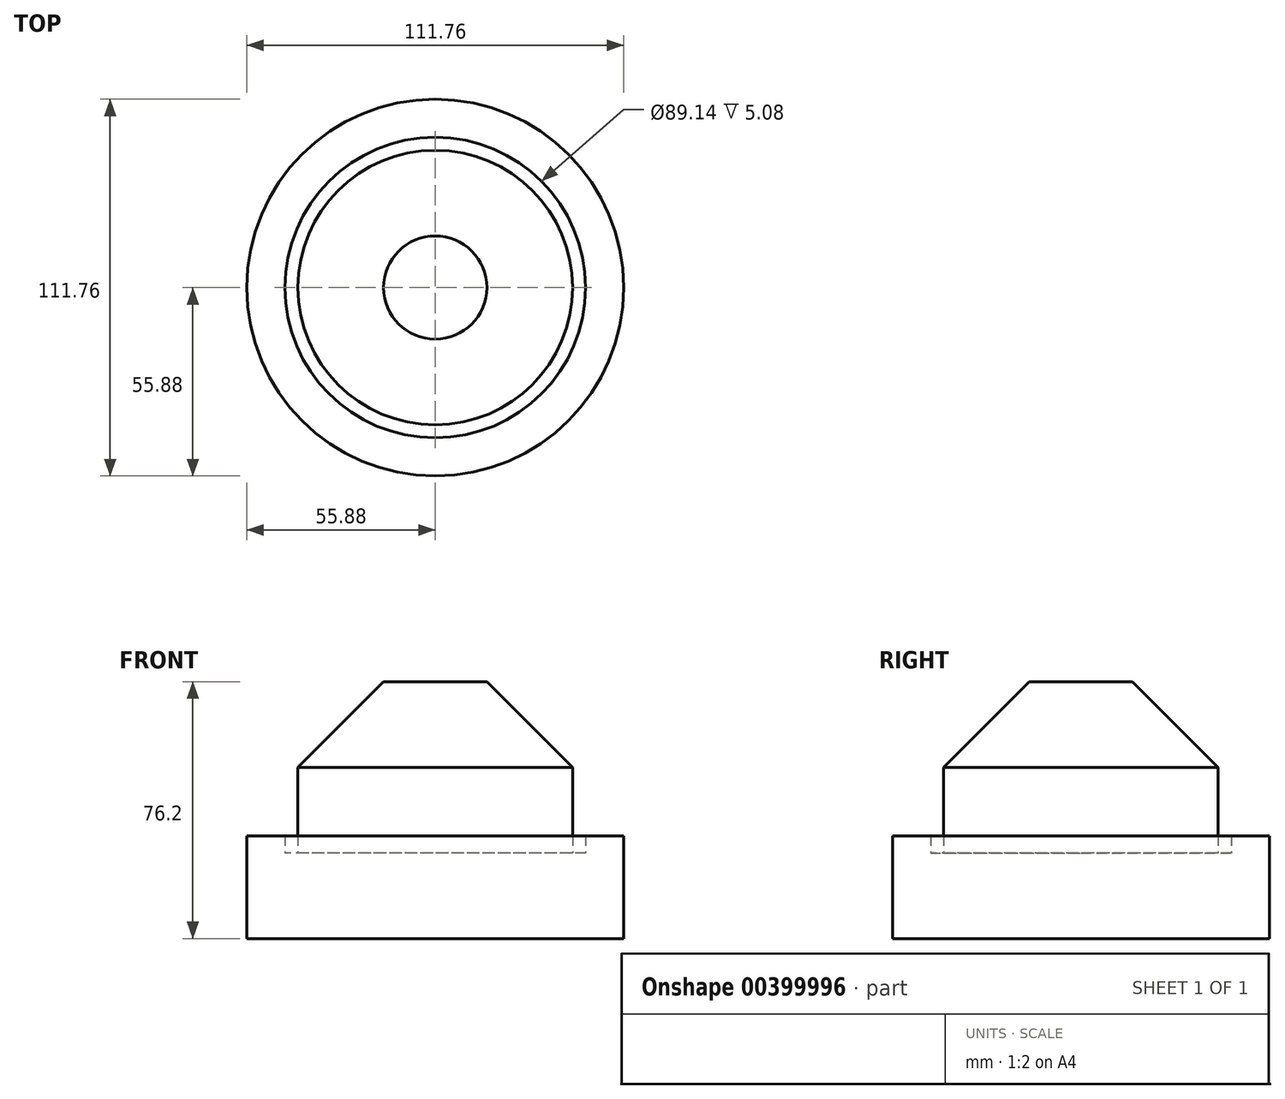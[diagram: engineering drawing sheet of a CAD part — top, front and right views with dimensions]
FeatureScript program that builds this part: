
annotation { "Feature Type Name" : "Feature", "Feature Type Description" : "" }
export const myFeature = defineFeature(function(context is Context, id is Id, definition is map)
    precondition{}
    {
        {
            var Q0;
            Q0=qCreatedBy(makeId("Top.planeOp"),FACE);
            var sketch = newSketch(context, id + "F0", { "sketchPlane" : qUnion([Q0])});
            skCircle(sketch, "E0", {"center": v(0, 0) * mm, "radius": 55.88 * mm});
            skSolve(sketch);
        }
        {
            var Q0;
            Q0 = qSketchRegion(id + "F0", true);
            extrude(context, id + "F1", {"entities" : qUnion([Q0]), "depth" : 25.4 * mm});
        }
        {
            var Q0;
            Q0=makeQuery(id+"F1.opExtrude","CAP_FACE",FACE,{"disambiguationData":[OSD([sQuery(id+"F0.wireOp",EDGE,"E0")])],"isStart":false});
            var sketch = newSketch(context, id + "F2", { "sketchPlane" : qUnion([Q0])});
            skCircle(sketch, "E1", {"center": v(0, 0) * mm, "radius": 44.57 * mm});
            skSolve(sketch);
        }
        {
            var Q0;
            Q0=makeQuery(id+"F2.imprint","IMPRINT",FACE,{"disambiguationData":[TD([[makeQuery(id+"F2.imprint","IMPRINT",EDGE,{"derivedFrom":sQuery(id+"F2.wireOp",EDGE,"E1")}),1.0]])]});
            var sketch = newSketch(context, id + "F3", { "sketchPlane" : qUnion([Q0])});
            skCircle(sketch, "E2", {"center": v(0, 0) * mm, "radius": 40.72 * mm});
            skSolve(sketch);
        }
        {
            var Q0;
            Q0=makeQuery(id+"F2.imprint","IMPRINT",FACE,{"disambiguationData":[TD([[makeQuery(id+"F2.imprint","IMPRINT",EDGE,{"derivedFrom":sQuery(id+"F2.wireOp",EDGE,"E1")}),-1.0]])]});
            extrude(context, id + "F4", {"entities" : qUnion([Q0]), "operationType" : NewBodyOperationType.ADD, "depth" : 5.08 * mm});
        }
        {
            var Q0;
            Q0=makeQuery(id+"F3.imprint","IMPRINT",FACE,{"disambiguationData":[TD([[makeQuery(id+"F3.imprint","IMPRINT",EDGE,{"derivedFrom":sQuery(id+"F3.wireOp",EDGE,"E2")}),1.0]])]});
            extrude(context, id + "F5", {"entities" : qUnion([Q0]), "operationType" : NewBodyOperationType.ADD, "depth" : 50.8 * mm});
        }
        {
            var Q0;
            Q0=makeQuery(id+"F5.opExtrude","CAP_EDGE",EDGE,{"disambiguationData":[OSD([sQuery(id+"F3.wireOp",EDGE,"E2")])],"isStart":false});
            chamfer(context, id + "F6", {"entities" : qUnion([Q0]), "width" : 25.4 * mm, "tangentPropagation" : true});
        }
    });
